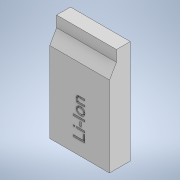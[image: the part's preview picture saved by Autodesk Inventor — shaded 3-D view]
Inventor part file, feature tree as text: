
AUTODESK INVENTOR PART (.ipt)
format: ipt  version: 2020 (Build 240168000, 168)  size: 167,424 bytes
history: native  units: mm
features: extrude x3, sketch x3, draft x1
ambient origin geometry x8: Origin, YZ Plane, XZ Plane, XY Plane, X Axis, Y Axis, Z Axis, Center Point
bodies: Solid1 (feature_tree)
feature tree (7):
  extrude  "Extrusion1"  Depth=26.0mm
  extrude  "Extrusion2"  Depth=35.0mm
  draft  "FaceDraft1"
  extrude  "Extrusion3"  TaperAngle=60.0deg  [1 undecoded]
  sketch  "Sketch1"  dims[d0=26.0mm d1=45.0mm]
  sketch  "Sketch2"  dims[d2=6.0mm d3=0.0mm d4=35.0mm]
  sketch  "Sketch3"  dims[d5=3.0mm d6=0.0mm d7=60.0deg d8=1.0mm d9=0.0mm]
note: 1 required parameter value undecoded (feature->parameter linkage not recoverable at this tier; creation-order binding heuristic only, values carry confidence <= 0.55)
